# Revit family: recesseddd
name_source: partatom
category: Lighting Fixtures
units: mm (PartAtom-declared; Revit-internal decimal feet)

## family parameters
Cut with Voids When Loaded = No
Host = Face
Light Source = Yes
OmniClass Number = 23.80.70.11
OmniClass Title = Luminaries for Internal Lighting
Part Type = Normal
Room Calculation Point = No
Round Connector Dimension = Use Diameter
Shared = No

## types (1)
- Not a Type - Load Type Catalog!
    Apparent Load = 0 VA
    Assembly Code = D5020200
    CRI = 80
    Color Filter = 16777215
    Default Elevation = 4' - 0"
    Description = Recessed Slim Beam
    Dimming Lamp Color Temperature Shift = <None>
    Edition number = 1
    Electrical Disconnect = Yes
    Emit Shape Visible in Rendering = No
    Emit from Rectangle Length = 3' - 11 1/2"
    Emit from Rectangle Width = 0' - 2"
    Frequency = 0 Hz
    Height = 0' - 3 1/2"
    Input Wattage = 0 W
    Keynote = 16500
    Lamp = LED
    Length = 4' - 0"
    Manufacturer = StarTek Lighting
    Number of Poles = 3
    Phase = 1
    Photometric Note = Import IES files https://starteklightingamerica.com
    Photometric Web File = Generic Light Source Shown : Please download and link the IES file that best matches your fixture specification
    Power Factor = 0.93
    Product Guid = 09d5efec-dccc-465b-9512-61c8981efa7c
    Product data url = https://www.bimobject.com
    Tilt Angle = 90.00°
    Type Comments = Linear Lighting Fixture
    URL = https://starteklightingamerica.com
    Voltage = 120 V
    Wattage Comments = Efficacy up to 116 lm/W
    Weight = 0.00 lbf
    Width = 0' - 2"
    z_DWCB = Mounting : Drywall with Cosmetic Bezzle (DWCB)
    z_DWSF = Mounting : Drywall with Spackle Flange (DWSF)
    z_End = Run : End Fixture
    z_Middle = Run : Middle Fixture
    z_STB = Mounting : 9/16" Screw Slotted T-BAR (STB1)
    z_Standalone = Run : Standalone Fixture
    z_Start = Run : Start Fixture
    z_Start Shape Closed = Run : Start Fixture for Closed Shapes
    z_TB1 = Mounting : 9/16" T-BAR (TB1)
    z_TB2 = Mounting : 15/16" T-BAR (TB2)
    z_TBT1 = Mounting : 9/16" T-BAR Tegular (TBT1)
    z_TBT2 = Mounting : 15/16" T-BAR Tegular (TBT2)

## geometry (parser evidence)
native form markers: Sweep x12
no freeform markers — native parametric forms only
